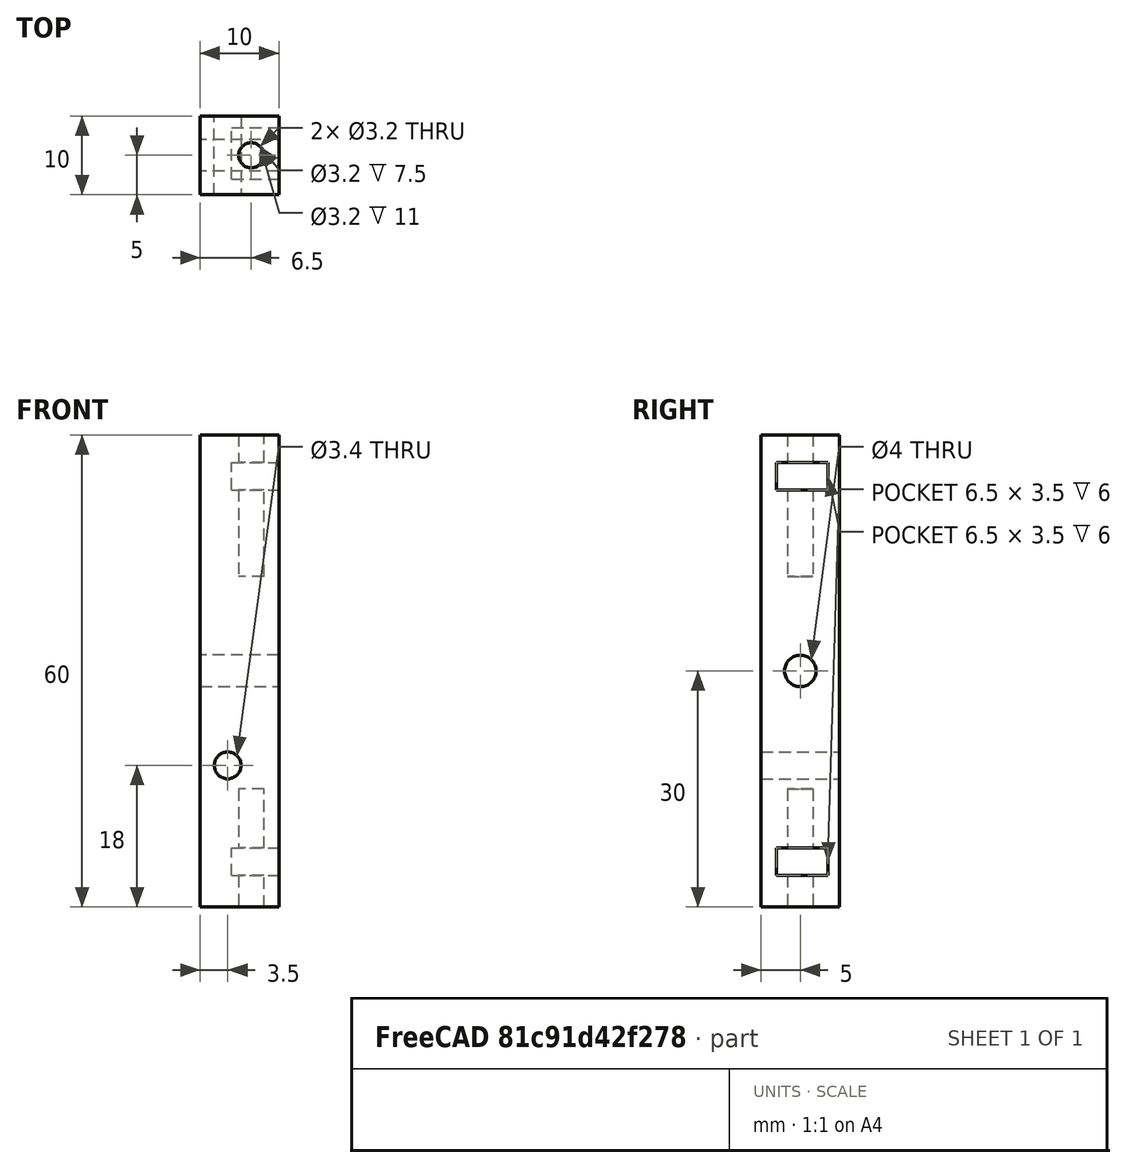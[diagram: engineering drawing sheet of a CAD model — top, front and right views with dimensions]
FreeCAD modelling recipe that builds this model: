
FCSTD DOCUMENT  (FreeCAD 0.21R33668 +26 (Git))
Label: columna
License: All rights reserved
LicenseURL: https://en.wikipedia.org/wiki/All_rights_reserved
objects: Part::Cylinder×4, Part::Box×3, Part::MultiFuse×1, Part::Cut×1, Mesh::Feature×1, Part::Feature×1
note: 10 computed .brp shape members not serialized (recipe doc carries the construction recipe); baked Part::Feature solids carry a one-line shape summary decoded from their .brp

FEATURE [Part::Box] Box015  label="Cubo015"
  AttacherType = Attacher::AttachEngine3D
  Height = 3.5
  Length = 10
  Placement = pos=(14,-41,-7) rot=(0,0,1;0rad)
  Width = 6.5
FEATURE [Part::Box] Box016  label="Cubo016"
  AttacherType = Attacher::AttachEngine3D
  Height = 3.5
  Length = 10
  Placement = pos=(14,-41,42) rot=(0,0,1;0rad)
  Width = 6.5
FEATURE [Part::Box] Box020  label="Cubo020"
  AttacherType = Attacher::AttachEngine3D
  Height = 60
  Length = 10
  Placement = pos=(10,-43,-11) rot=(0,0,1;0rad)
  Width = 10
FEATURE [Part::Cylinder] Cylinder053  label="Cilindro053"
  Angle = 360
  AttacherType = Attacher::AttachEngine3D
  FirstAngle = 0
  Height = 20
  Placement = pos=(16.5,-38,31) rot=(0,0,1;0rad)
  Radius = 1.6
  SecondAngle = 0
FEATURE [Part::Cylinder] Cylinder058  label="Cilindro058"
  Angle = 360
  AttacherType = Attacher::AttachEngine3D
  FirstAngle = 0
  Height = 150
  Placement = pos=(13.5,50,7) rot=(1,0,0;1.5708rad)
  Radius = 1.7
  SecondAngle = 0
FEATURE [Part::Cylinder] Cylinder059  label="Cilindro059"
  Angle = 360
  AttacherType = Attacher::AttachEngine3D
  FirstAngle = 0
  Height = 20
  Placement = pos=(16.5,-38,-16) rot=(0,0,1;0rad)
  Radius = 1.6
  SecondAngle = 0
FEATURE [Part::Cylinder] Cylinder  label="Cilindro"
  Angle = 360
  AttacherType = Attacher::AttachEngine3D
  FirstAngle = 0
  Height = 30
  Placement = pos=(1,-38,19) rot=(0,1,0;1.5708rad)
  Radius = 2
  SecondAngle = 0
FEATURE [Part::MultiFuse] Fusion
  Shapes = -> [Box015,Box016,Cylinder053,Cylinder058,Cylinder059,Cylinder]
FEATURE [Part::Cut] Cut  label="columna"
  Base = -> Box020
  Tool = -> Fusion
FEATURE [Mesh::Feature] Mesh  label="columna (Meshed)"
FEATURE [Part::Feature] Cut_solid  label="columna (Solid)"
  shape: bbox 10 x 10 x 60 mm, 24 faces (baked)
